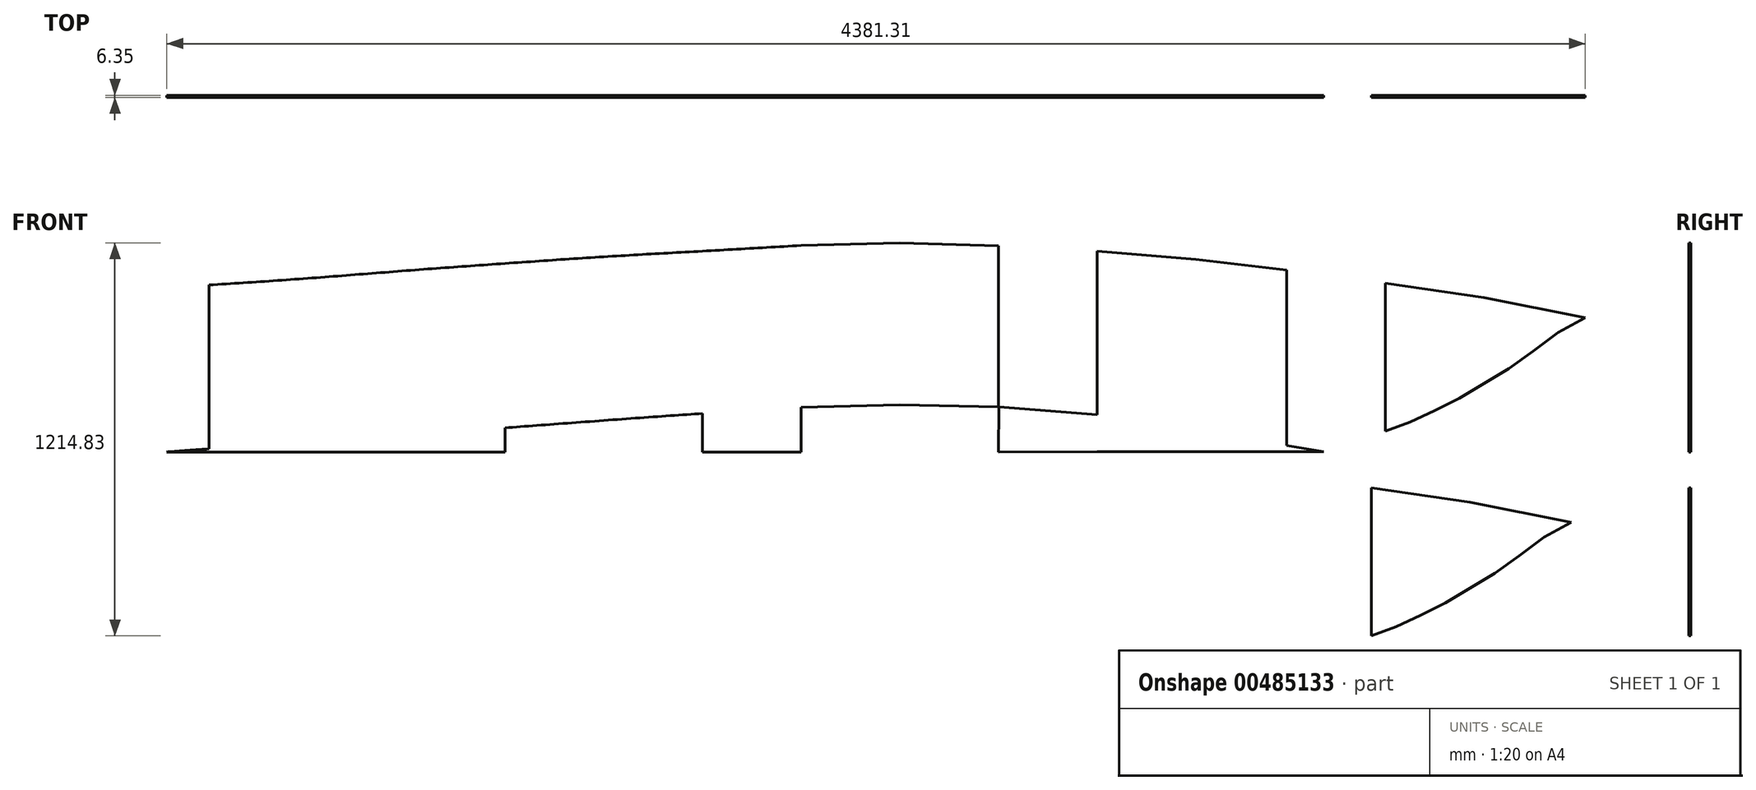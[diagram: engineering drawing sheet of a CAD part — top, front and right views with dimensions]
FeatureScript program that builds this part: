
annotation { "Feature Type Name" : "Feature", "Feature Type Description" : "" }
export const myFeature = defineFeature(function(context is Context, id is Id, definition is map)
    precondition{}
    {
        {
            var Q0;
            Q0=qCreatedBy(makeId("Front.planeOp"),FACE);
            var sketch = newSketch(context, id + "F0", { "sketchPlane" : qUnion([Q0])});
            skLineSegment(sketch, "E0.bottom", {"start": v(-1219.2, 573.09) * mm, "end": v(1219.2, 573.09) * mm});
            skLineSegment(sketch, "E0.top", {"start": v(-1219.2, -646.11) * mm, "end": v(1219.2, -646.11) * mm});
            skLineSegment(sketch, "E0.left", {"start": v(-1219.2, 573.09) * mm, "end": v(-1219.2, -646.11) * mm});
            skLineSegment(sketch, "E1", {"start": v(1219.2, -646.11) * mm, "end": v(1219.2, -7.94) * mm});
            skLineSegment(sketch, "E2", {"start": v(1219.2, -646.11) * mm, "end": v(1219.2, -508) * mm});
            skLineSegment(sketch, "E3", {"start": v(1219.2, 573.09) * mm, "end": v(914.4, 573.09) * mm});
            skLineSegment(sketch, "E4", {"start": v(914.4, 573.09) * mm, "end": v(609.6, 573.09) * mm});
            skLineSegment(sketch, "E5", {"start": v(609.6, 573.09) * mm, "end": v(304.8, 573.09) * mm});
            skLineSegment(sketch, "E6", {"start": v(304.8, 573.09) * mm, "end": v(0, 573.09) * mm});
            skLineSegment(sketch, "E7", {"start": v(0, 573.09) * mm, "end": v(-304.8, 573.09) * mm});
            skLineSegment(sketch, "E8", {"start": v(-304.8, 573.09) * mm, "end": v(-609.6, 573.09) * mm});
            skLineSegment(sketch, "E9", {"start": v(-609.6, 573.09) * mm, "end": v(-914.4, 573.09) * mm});
            skLineSegment(sketch, "E10", {"start": v(-914.4, 573.09) * mm, "end": v(-1219.2, 573.09) * mm});
            skLineSegment(sketch, "E11", {"start": v(914.4, -646.11) * mm, "end": v(914.4, -25.4) * mm});
            skLineSegment(sketch, "E12", {"start": v(609.6, -646.11) * mm, "end": v(609.6, -42.86) * mm});
            skLineSegment(sketch, "E13", {"start": v(304.8, -646.11) * mm, "end": v(304.8, -63.5) * mm});
            skLineSegment(sketch, "E14", {"start": v(-304.8, -646.11) * mm, "end": v(-304.8, -109.54) * mm});
            skLineSegment(sketch, "E15", {"start": v(-609.6, -646.11) * mm, "end": v(-609.6, -130.18) * mm});
            skFitSpline(sketch, "E16", {"points": [v(1219.2, -7.94) * mm, v(914.4, -25.4) * mm, v(609.6, -42.86) * mm, v(304.8, -63.5) * mm, v(0, -85.73) * mm, v(-304.8, -109.54) * mm, v(-609.6, -130.18) * mm], "startDerivative": vector(-1829.33, -106.06) * mm, "endDerivative": vector(-1828.98, -118.14) * mm});
            skLineSegment(sketch, "E17", {"start": v(-914.4, -646.11) * mm, "end": v(-739.77, -646.11) * mm});
            skLineSegment(sketch, "E18", {"start": v(-914.4, -143.6) * mm, "end": v(-819.15, -143.6) * mm});
            skLineSegment(sketch, "E19", {"start": v(-739.77, -646.11) * mm, "end": v(-819.15, -143.6) * mm});
            skLineSegment(sketch, "E20", {"start": v(-609.6, -130.18) * mm, "end": v(-819.15, -143.6) * mm});
            skLineSegment(sketch, "E21", {"start": v(-609.6, -646.11) * mm, "end": v(-609.6, -636.59) * mm});
            skLineSegment(sketch, "E22", {"start": v(-304.8, -646.11) * mm, "end": v(-304.8, -614.36) * mm});
            skLineSegment(sketch, "E23", {"start": v(304.8, -646.11) * mm, "end": v(304.8, -571.5) * mm});
            skLineSegment(sketch, "E24", {"start": v(0, -646.11) * mm, "end": v(0, -85.73) * mm});
            skLineSegment(sketch, "E25", {"start": v(0, -646.11) * mm, "end": v(0, -593.73) * mm});
            skLineSegment(sketch, "E26", {"start": v(609.6, -646.11) * mm, "end": v(609.6, -560.39) * mm});
            skLineSegment(sketch, "E27", {"start": v(914.4, -646.11) * mm, "end": v(914.4, -527.05) * mm});
            skFitSpline(sketch, "E28", {"points": [v(-739.77, -646.11) * mm, v(-609.6, -636.59) * mm, v(-304.8, -614.36) * mm, v(0, -593.73) * mm, v(304.8, -571.5) * mm, v(914.4, -527.05) * mm, v(1219.2, -508) * mm], "startDerivative": vector(1074.2, 78.02) * mm, "endDerivative": vector(1622.5, 94.88) * mm});
            skLineSegment(sketch, "E29", {"start": v(1219.2, 573.09) * mm, "end": v(3657.6, 573.09) * mm});
            skLineSegment(sketch, "E30", {"start": v(3657.6, 573.09) * mm, "end": v(3633.5, -645.87) * mm});
            skLineSegment(sketch, "E31", {"start": v(1219.2, 573.09) * mm, "end": v(1524, 573.09) * mm});
            skLineSegment(sketch, "E32", {"start": v(1524, 573.09) * mm, "end": v(1828.8, 573.09) * mm});
            skLineSegment(sketch, "E33", {"start": v(1828.8, 573.09) * mm, "end": v(2133.6, 573.09) * mm});
            skLineSegment(sketch, "E34", {"start": v(2133.6, 573.09) * mm, "end": v(2438.4, 573.09) * mm});
            skLineSegment(sketch, "E35", {"start": v(2438.4, 573.09) * mm, "end": v(2743.2, 573.09) * mm});
            skLineSegment(sketch, "E36", {"start": v(2743.2, 573.09) * mm, "end": v(3048, 573.09) * mm});
            skLineSegment(sketch, "E37", {"start": v(3048, 573.09) * mm, "end": v(3352.8, 573.09) * mm});
            skLineSegment(sketch, "E38", {"start": v(3352.8, 573.09) * mm, "end": v(3657.6, 573.09) * mm});
            skLineSegment(sketch, "E39", {"start": v(1524, -646.11) * mm, "end": v(1524, 0) * mm});
            skLineSegment(sketch, "E40", {"start": v(1524, -646.11) * mm, "end": v(1524, -500.06) * mm});
            skLineSegment(sketch, "E41", {"start": v(1219.2, -7.94) * mm, "end": v(1524, 0) * mm});
            skLineSegment(sketch, "E42", {"start": v(1219.2, -508) * mm, "end": v(1524, -500.06) * mm});
            skLineSegment(sketch, "E43", {"start": v(1828.8, -646.96) * mm, "end": v(1828.8, -8.78) * mm});
            skLineSegment(sketch, "E44", {"start": v(1219.2, -646.11) * mm, "end": v(1828.8, -646.96) * mm});
            skLineSegment(sketch, "E45", {"start": v(1828.8, -646.96) * mm, "end": v(2133.6, -645.87) * mm});
            skLineSegment(sketch, "E46", {"start": v(2133.6, -645.87) * mm, "end": v(3633.5, -645.87) * mm});
            skLineSegment(sketch, "E47", {"start": v(1524, 0) * mm, "end": v(1828.8, -8.78) * mm});
            skLineSegment(sketch, "E48", {"start": v(1828.8, -646.96) * mm, "end": v(1828.8, -507.26) * mm});
            skLineSegment(sketch, "E49", {"start": v(1524, -500.06) * mm, "end": v(1828.8, -507.26) * mm});
            skLineSegment(sketch, "E50", {"start": v(2133.6, -645.87) * mm, "end": v(2133.6, -25.16) * mm});
            skLineSegment(sketch, "E51", {"start": v(2133.6, -645.87) * mm, "end": v(2133.6, -531.57) * mm});
            skLineSegment(sketch, "E52", {"start": v(1828.8, -8.78) * mm, "end": v(2133.6, -25.16) * mm});
            skLineSegment(sketch, "E53", {"start": v(1829.9, -507.26) * mm, "end": v(2133.6, -531.57) * mm});
            skLineSegment(sketch, "E54", {"start": v(2438.4, -646.11) * mm, "end": v(2438.4, -50.8) * mm});
            skLineSegment(sketch, "E55", {"start": v(2438.4, -646.11) * mm, "end": v(2438.4, -573.09) * mm});
            skLineSegment(sketch, "E56", {"start": v(2133.6, -531.57) * mm, "end": v(2438.4, -573.09) * mm});
            skLineSegment(sketch, "E57", {"start": v(2133.6, -25.16) * mm, "end": v(2438.4, -50.8) * mm});
            skLineSegment(sketch, "E58", {"start": v(2718.93, -645.87) * mm, "end": v(2718.93, -83.9) * mm});
            skLineSegment(sketch, "E59", {"start": v(2718.93, -645.87) * mm, "end": v(2718.93, -626.82) * mm});
            skLineSegment(sketch, "E60", {"start": v(2438.4, -573.09) * mm, "end": v(2718.93, -626.82) * mm});
            skLineSegment(sketch, "E61", {"start": v(2438.4, -50.8) * mm, "end": v(2718.93, -83.9) * mm});
            skLineSegment(sketch, "E62", {"start": v(2718.93, -645.87) * mm, "end": v(2833.23, -645.87) * mm});
            skLineSegment(sketch, "E63", {"start": v(2718.93, -626.82) * mm, "end": v(2833.23, -645.87) * mm});
            skLineSegment(sketch, "E64", {"start": v(2833.23, -645.87) * mm, "end": v(2947.53, -645.87) * mm});
            skLineSegment(sketch, "E65", {"start": v(2947.53, -645.87) * mm, "end": v(3023.73, -645.87) * mm});
            skLineSegment(sketch, "E66", {"start": v(3023.73, -645.87) * mm, "end": v(3099.93, -645.87) * mm});
            skLineSegment(sketch, "E67", {"start": v(3099.93, -645.87) * mm, "end": v(3176.13, -645.87) * mm});
            skLineSegment(sketch, "E68", {"start": v(3176.13, -645.87) * mm, "end": v(3252.33, -645.87) * mm});
            skLineSegment(sketch, "E69", {"start": v(3252.33, -645.87) * mm, "end": v(3328.53, -645.87) * mm});
            skLineSegment(sketch, "E70", {"start": v(3328.53, -645.87) * mm, "end": v(3404.73, -645.87) * mm});
            skLineSegment(sketch, "E71", {"start": v(3404.73, -645.87) * mm, "end": v(3480.93, -645.87) * mm});
            skLineSegment(sketch, "E72", {"start": v(3480.93, -645.87) * mm, "end": v(3557.13, -645.87) * mm});
            skLineSegment(sketch, "E73", {"start": v(3557.13, -645.87) * mm, "end": v(3633.33, -645.87) * mm});
            skLineSegment(sketch, "E74", {"start": v(3633.33, -645.87) * mm, "end": v(3633.5, -645.87) * mm});
            skLineSegment(sketch, "E75", {"start": v(2947.53, -645.87) * mm, "end": v(2947.53, -609.36) * mm});
            skLineSegment(sketch, "E76", {"start": v(3023.73, -645.87) * mm, "end": v(3023.73, -582.37) * mm});
            skLineSegment(sketch, "E77", {"start": v(3099.93, -645.87) * mm, "end": v(3099.93, -553.8) * mm});
            skLineSegment(sketch, "E78", {"start": v(3176.13, -645.87) * mm, "end": v(3176.13, -518.87) * mm});
            skLineSegment(sketch, "E79", {"start": v(3252.33, -645.87) * mm, "end": v(3252.33, -480.77) * mm});
            skLineSegment(sketch, "E80", {"start": v(3328.53, -645.87) * mm, "end": v(3328.53, -434.74) * mm});
            skLineSegment(sketch, "E81", {"start": v(3404.73, -645.87) * mm, "end": v(3404.73, -388.7) * mm});
            skLineSegment(sketch, "E82", {"start": v(3480.93, -645.87) * mm, "end": v(3480.93, -334.72) * mm});
            skLineSegment(sketch, "E83", {"start": v(3557.13, -645.87) * mm, "end": v(3557.13, -277.57) * mm});
            skLineSegment(sketch, "E84", {"start": v(3633.33, -645.87) * mm, "end": v(3641.53, -231.52) * mm});
            skLineSegment(sketch, "E85", {"start": v(3023.73, -645.87) * mm, "end": v(3023.73, -125.17) * mm});
            skLineSegment(sketch, "E86", {"start": v(2718.93, -83.9) * mm, "end": v(3023.73, -125.17) * mm});
            skLineSegment(sketch, "E87", {"start": v(3328.53, -645.87) * mm, "end": v(3328.53, -169.62) * mm});
            skLineSegment(sketch, "E88", {"start": v(2833.23, -645.87) * mm, "end": v(2947.53, -609.36) * mm});
            skLineSegment(sketch, "E89", {"start": v(2947.53, -609.36) * mm, "end": v(3023.73, -582.37) * mm});
            skLineSegment(sketch, "E90", {"start": v(3023.73, -582.37) * mm, "end": v(3099.93, -553.8) * mm});
            skLineSegment(sketch, "E91", {"start": v(3099.93, -553.8) * mm, "end": v(3176.13, -518.87) * mm});
            skLineSegment(sketch, "E92", {"start": v(3252.33, -480.77) * mm, "end": v(3328.53, -434.74) * mm});
            skLineSegment(sketch, "E93", {"start": v(3328.53, -434.74) * mm, "end": v(3404.73, -388.7) * mm});
            skLineSegment(sketch, "E94", {"start": v(3404.73, -388.7) * mm, "end": v(3480.93, -334.72) * mm});
            skLineSegment(sketch, "E95", {"start": v(3480.93, -334.72) * mm, "end": v(3557.13, -277.57) * mm});
            skLineSegment(sketch, "E96", {"start": v(3641.53, -231.52) * mm, "end": v(3557.13, -277.57) * mm});
            skLineSegment(sketch, "E97", {"start": v(3023.73, -125.17) * mm, "end": v(3328.53, -169.62) * mm});
            skLineSegment(sketch, "E98", {"start": v(3328.53, -169.62) * mm, "end": v(3641.53, -231.52) * mm});
            skLineSegment(sketch, "E99", {"start": v(1828.8, -646.96) * mm, "end": v(1829.9, -507.26) * mm});
            skLineSegment(sketch, "E100", {"start": v(3176.13, -518.87) * mm, "end": v(3252.33, -480.77) * mm});
            skSolve(sketch);
        }
        {
            var Q0;
            {var subQ0=sQuery(id+"F0.wireOp",EDGE,"E90");Q0=makeQuery(id+"F0.imprint","IMPRINT",FACE,{"disambiguationData":[TD([[makeQuery(id+"F0.imprint","IMPRINT",EDGE,{"derivedFrom":subQ0}),1.0]])]});}
            var Q1;
            {var subQ0=sQuery(id+"F0.wireOp",EDGE,"E93");Q1=makeQuery(id+"F0.imprint","IMPRINT",FACE,{"disambiguationData":[TD([[makeQuery(id+"F0.imprint","IMPRINT",EDGE,{"derivedFrom":subQ0}),1.0]])]});}
            var Q2;
            Q2=makeQuery(id+"F0.imprint","IMPRINT",FACE,{"disambiguationData":[TD([[makeQuery(id+"F0.imprint","IMPRINT",EDGE,{"derivedFrom":sQuery(id+"F0.wireOp",EDGE,"E58")}),-1.0]])]});
            var Q3;
            Q3=makeQuery(id+"F0.imprint","IMPRINT",FACE,{"disambiguationData":[TD([[makeQuery(id+"F0.imprint","IMPRINT",EDGE,{"derivedFrom":sQuery(id+"F0.wireOp",EDGE,"E54")}),-1.0]])]});
            var Q4;
            Q4=makeQuery(id+"F0.imprint","IMPRINT",FACE,{"disambiguationData":[TD([[makeQuery(id+"F0.imprint","IMPRINT",EDGE,{"derivedFrom":sQuery(id+"F0.wireOp",EDGE,"E50")}),-1.0]])]});
            var Q5;
            Q5=makeQuery(id+"F0.imprint","IMPRINT",FACE,{"disambiguationData":[TD([[makeQuery(id+"F0.imprint","IMPRINT",EDGE,{"derivedFrom":sQuery(id+"F0.wireOp",EDGE,"E50")}),1.0]])]});
            var Q6;
            Q6=makeQuery(id+"F0.imprint","IMPRINT",FACE,{"disambiguationData":[TD([[makeQuery(id+"F0.imprint","IMPRINT",EDGE,{"derivedFrom":sQuery(id+"F0.wireOp",EDGE,"E39")}),-1.0]])]});
            var Q7;
            Q7=makeQuery(id+"F0.imprint","IMPRINT",FACE,{"disambiguationData":[TD([[makeQuery(id+"F0.imprint","IMPRINT",EDGE,{"derivedFrom":sQuery(id+"F0.wireOp",EDGE,"E1")}),-1.0]])]});
            var Q8;
            {var subQ0=sQuery(id+"F0.wireOp",EDGE,"E1");Q8=makeQuery(id+"F0.imprint","IMPRINT",FACE,{"disambiguationData":[TD([[makeQuery(id+"F0.imprint","IMPRINT",EDGE,{"derivedFrom":subQ0}),1.0]])]});}
            var Q9;
            {var subQ0=sQuery(id+"F0.wireOp",EDGE,"E11");Q9=makeQuery(id+"F0.imprint","IMPRINT",FACE,{"disambiguationData":[TD([[makeQuery(id+"F0.imprint","IMPRINT",EDGE,{"derivedFrom":subQ0}),1.0]])]});}
            var Q10;
            {var subQ5=sQuery(id+"F0.wireOp",EDGE,"E13");Q10=makeQuery(id+"F0.imprint","IMPRINT",FACE,{"disambiguationData":[TD([[makeQuery(id+"F0.imprint","IMPRINT",EDGE,{"derivedFrom":subQ5}),-1.0]])]});}
            var Q11;
            {var subQ0=sQuery(id+"F0.wireOp",EDGE,"E13");Q11=makeQuery(id+"F0.imprint","IMPRINT",FACE,{"disambiguationData":[TD([[makeQuery(id+"F0.imprint","IMPRINT",EDGE,{"derivedFrom":subQ0}),1.0]])]});}
            var Q12;
            {var subQ0=sQuery(id+"F0.wireOp",EDGE,"E14");Q12=makeQuery(id+"F0.imprint","IMPRINT",FACE,{"disambiguationData":[TD([[makeQuery(id+"F0.imprint","IMPRINT",EDGE,{"derivedFrom":subQ0}),-1.0]])]});}
            var Q13;
            {var subQ0=sQuery(id+"F0.wireOp",EDGE,"E14");Q13=makeQuery(id+"F0.imprint","IMPRINT",FACE,{"disambiguationData":[TD([[makeQuery(id+"F0.imprint","IMPRINT",EDGE,{"derivedFrom":subQ0}),1.0]])]});}
            var Q14;
            {var subQ0=sQuery(id+"F0.wireOp",EDGE,"E15");Q14=makeQuery(id+"F0.imprint","IMPRINT",FACE,{"disambiguationData":[TD([[makeQuery(id+"F0.imprint","IMPRINT",EDGE,{"derivedFrom":subQ0}),1.0]])]});}
            extrude(context, id + "F1", {"entities" : qUnion([Q0, Q1, Q2, Q3, Q4, Q5, Q6, Q7, Q8, Q9, Q10, Q11, Q12, Q13, Q14]), "depth" : 6.35 * mm});
        }
        {
            var Q0;
            Q0=makeQuery(id+"F1.opExtrude","SWEPT_BODY",BODY,{"disambiguationData":[OSD([sQuery(id+"F0.wireOp",EDGE,"E16"),sQuery(id+"F0.wireOp",EDGE,"E19"),sQuery(id+"F0.wireOp",EDGE,"E20"),sQuery(id+"F0.wireOp",EDGE,"E28"),sQuery(id+"F0.wireOp",EDGE,"E41"),sQuery(id+"F0.wireOp",EDGE,"E42"),sQuery(id+"F0.wireOp",EDGE,"E47"),sQuery(id+"F0.wireOp",EDGE,"E49"),sQuery(id+"F0.wireOp",EDGE,"E52"),sQuery(id+"F0.wireOp",EDGE,"E53"),sQuery(id+"F0.wireOp",EDGE,"E56"),sQuery(id+"F0.wireOp",EDGE,"E57"),sQuery(id+"F0.wireOp",EDGE,"E60"),sQuery(id+"F0.wireOp",EDGE,"E61"),sQuery(id+"F0.wireOp",EDGE,"E63"),sQuery(id+"F0.wireOp",EDGE,"E86"),sQuery(id+"F0.wireOp",EDGE,"E88"),sQuery(id+"F0.wireOp",EDGE,"E89"),sQuery(id+"F0.wireOp",EDGE,"E90"),sQuery(id+"F0.wireOp",EDGE,"E91"),sQuery(id+"F0.wireOp",EDGE,"E92"),sQuery(id+"F0.wireOp",EDGE,"E93"),sQuery(id+"F0.wireOp",EDGE,"E94"),sQuery(id+"F0.wireOp",EDGE,"E95"),sQuery(id+"F0.wireOp",EDGE,"E96"),sQuery(id+"F0.wireOp",EDGE,"E97"),sQuery(id+"F0.wireOp",EDGE,"E98"),sQuery(id+"F0.wireOp",EDGE,"E99"),sQuery(id+"F0.wireOp",EDGE,"E43"),sQuery(id+"F0.wireOp",EDGE,"E100")])]});
            transform(context, id + "F2", {"entities" : qUnion([Q0]), "transformType" : TransformType.TRANSLATION_3D, "dx" : -43.18 * mm, "dy" : 0 * mm, "dz" : -632.46 * mm, "makeCopy" : true});
        }
    });
